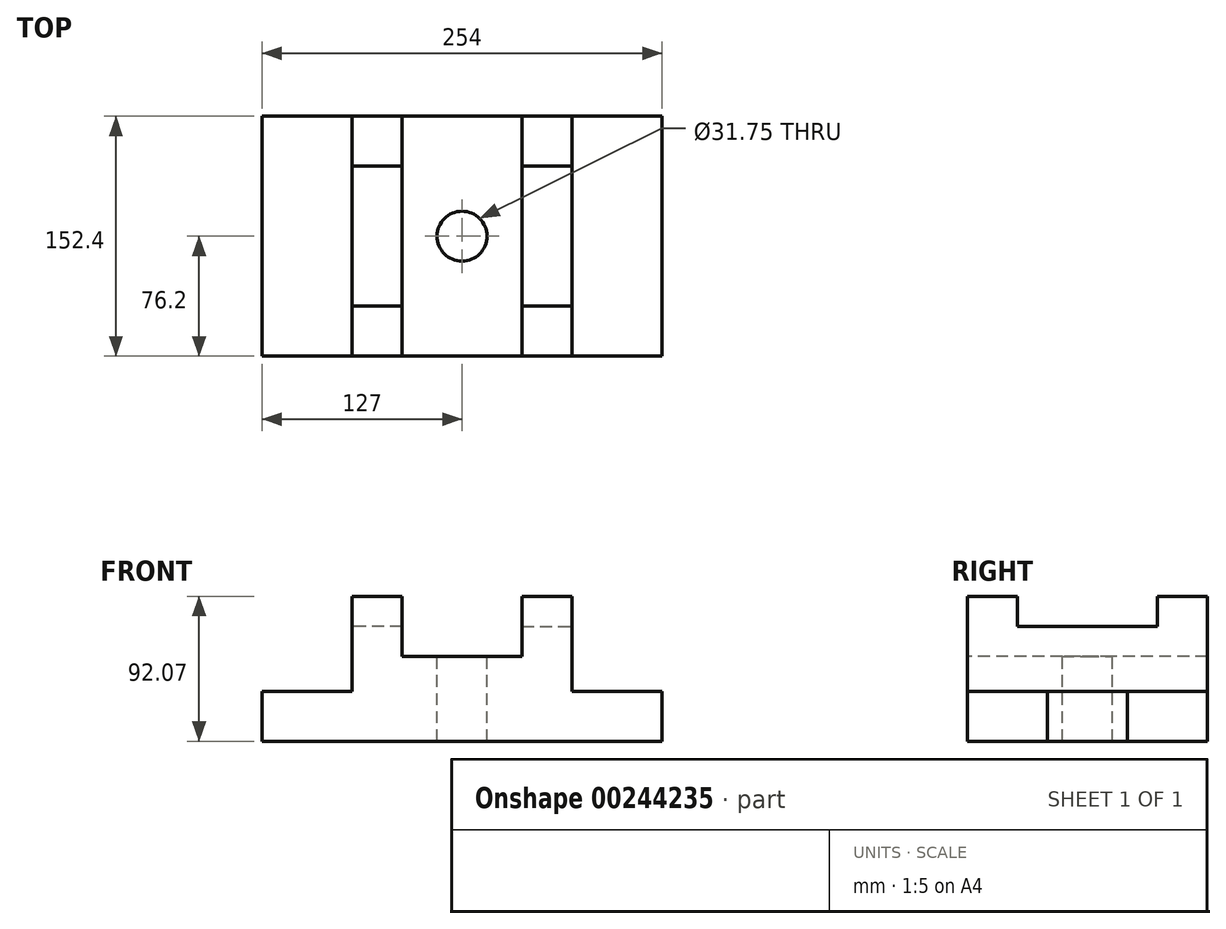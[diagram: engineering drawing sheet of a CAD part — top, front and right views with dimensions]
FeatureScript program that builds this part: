
annotation { "Feature Type Name" : "Feature", "Feature Type Description" : "" }
export const myFeature = defineFeature(function(context is Context, id is Id, definition is map)
    precondition{}
    {
        {
            var Q0;
            Q0=qCreatedBy(makeId("Front.planeOp"),FACE);
            var sketch = newSketch(context, id + "F0", { "sketchPlane" : qUnion([Q0])});
            skLineSegment(sketch, "E0.bottom", {"start": v(127, 15.88) * mm, "end": v(-127, 15.88) * mm});
            skLineSegment(sketch, "E0.top", {"start": v(127, -15.88) * mm, "end": v(-127, -15.88) * mm});
            skLineSegment(sketch, "E0.left", {"start": v(127, 15.88) * mm, "end": v(127, -15.88) * mm});
            skLineSegment(sketch, "E0.right", {"start": v(-127, 15.88) * mm, "end": v(-127, -15.88) * mm});
            skPoint(sketch, "E0.middle", {"position": v(0, 0) * mm});
            skSolve(sketch);
        }
        {
            var Q0;
            Q0=makeQuery(id+"F0.imprint","IMPRINT",FACE,{"disambiguationData":[TD([[makeQuery(id+"F0.imprint","IMPRINT",EDGE,{"derivedFrom":sQuery(id+"F0.wireOp",EDGE,"E0.bottom")}),1.0]])]});
            extrude(context, id + "F1", {"entities" : qUnion([Q0]), "depth" : 152.4 * mm});
        }
        {
            var Q0;
            Q0=makeQuery(id+"F1.opExtrude","SWEPT_FACE",FACE,{"disambiguationData":[OSD([sQuery(id+"F0.wireOp",EDGE,"E0.top")])]});
            extrude(context, id + "F2", {"entities" : qUnion([Q0]), "operationType" : NewBodyOperationType.ADD, "depth" : 92.07 * mm});
        }
        {
            var Q0;
            Q0=makeQuery(id+"F1.opExtrude","SWEPT_FACE",FACE,{"disambiguationData":[OSD([sQuery(id+"F0.wireOp",EDGE,"E0.bottom")])]});
            extrude(context, id + "F3", {"entities" : qUnion([Q0]), "operationType" : NewBodyOperationType.REMOVE, "oppositeDirection" : true, "depth" : 31.75 * mm});
        }
        {
            var Q0;
            Q0=makeQuery(id+"F3.boolean.opBoolean","COPY",FACE,{"derivedFrom":makeQuery(id+"F3.opExtrude","CAP_FACE",FACE,{"disambiguationData":[OSD([sQuery(id+"F0.wireOp",EDGE,"E0.bottom")])],"isStart":false})});
            var sketch = newSketch(context, id + "F4", { "sketchPlane" : qUnion([Q0])});
            skLineSegment(sketch, "E1", {"start": v(-127, 0) * mm, "end": v(-69.85, 0) * mm});
            skLineSegment(sketch, "E2", {"start": v(-69.85, -152.4) * mm, "end": v(-69.85, 0) * mm});
            skSolve(sketch);
        }
        {
            var Q0;
            Q0=makeQuery(id+"F4.imprint","IMPRINT",FACE,{"disambiguationData":[TD([[makeQuery(id+"F4.imprint","IMPRINT",EDGE,{"derivedFrom":sQuery(id+"F4.wireOp",EDGE,"E1")}),1.0]])]});
            extrude(context, id + "F5", {"entities" : qUnion([Q0]), "operationType" : NewBodyOperationType.REMOVE, "oppositeDirection" : true, "depth" : 59.05 * mm});
        }
        {
            var Q0;
            Q0=makeQuery(id+"F3.boolean.opBoolean","COPY",FACE,{"derivedFrom":makeQuery(id+"F3.opExtrude","CAP_FACE",FACE,{"disambiguationData":[OSD([sQuery(id+"F0.wireOp",EDGE,"E0.bottom")])],"isStart":false})});
            var sketch = newSketch(context, id + "F6", { "sketchPlane" : qUnion([Q0])});
            skLineSegment(sketch, "E3", {"start": v(-69.85, 0) * mm, "end": v(-38.1, 0) * mm});
            skLineSegment(sketch, "E4.bottom", {"start": v(-38.1, 0) * mm, "end": v(38.1, 0) * mm});
            skLineSegment(sketch, "E4.top", {"start": v(-38.1, -152.4) * mm, "end": v(38.1, -152.4) * mm});
            skLineSegment(sketch, "E4.left", {"start": v(-38.1, 0) * mm, "end": v(-38.1, -152.4) * mm});
            skLineSegment(sketch, "E4.right", {"start": v(38.1, 0) * mm, "end": v(38.1, -152.4) * mm});
            skSolve(sketch);
        }
        {
            var Q0;
            Q0=makeQuery(id+"F6.imprint","IMPRINT",FACE,{"disambiguationData":[TD([[makeQuery(id+"F6.imprint","IMPRINT",EDGE,{"derivedFrom":sQuery(id+"F6.wireOp",EDGE,"E4.bottom")}),1.0]])]});
            extrude(context, id + "F7", {"entities" : qUnion([Q0]), "operationType" : NewBodyOperationType.REMOVE, "oppositeDirection" : true, "depth" : 38.1 * mm});
        }
        {
            var Q0;
            {var subQ0=sQuery(id+"F0.wireOp",EDGE,"E0.left");var subQ3=sQuery(id+"F0.wireOp",EDGE,"E0.bottom");Q0=makeQuery(id+"F7.boolean.opBoolean","SPLIT",FACE,{"disambiguationData":[TD([makeQuery(id+"F1.opExtrude","SWEPT_FACE",FACE,{"disambiguationData":[OSD([subQ0])]})])],"derivedFrom":makeQuery(id+"F3.boolean.opBoolean","COPY",FACE,{"derivedFrom":makeQuery(id+"F3.opExtrude","CAP_FACE",FACE,{"disambiguationData":[OSD([subQ3])],"isStart":false})})});}
            var sketch = newSketch(context, id + "F8", { "sketchPlane" : qUnion([Q0])});
            skLineSegment(sketch, "E5", {"start": v(38.1, 0) * mm, "end": v(69.85, 0) * mm});
            skLineSegment(sketch, "E6.bottom", {"start": v(69.85, 0) * mm, "end": v(127, 0) * mm});
            skLineSegment(sketch, "E6.top", {"start": v(69.85, -152.4) * mm, "end": v(127, -152.4) * mm});
            skLineSegment(sketch, "E6.left", {"start": v(69.85, 0) * mm, "end": v(69.85, -152.4) * mm});
            skLineSegment(sketch, "E6.right", {"start": v(127, 0) * mm, "end": v(127, -152.4) * mm});
            skSolve(sketch);
        }
        {
            var Q0;
            Q0=makeQuery(id+"F8.imprint","IMPRINT",FACE,{"disambiguationData":[TD([[makeQuery(id+"F8.imprint","IMPRINT",EDGE,{"derivedFrom":sQuery(id+"F8.wireOp",EDGE,"E6.bottom")}),1.0]])]});
            extrude(context, id + "F9", {"entities" : qUnion([Q0]), "operationType" : NewBodyOperationType.REMOVE, "oppositeDirection" : true, "depth" : 60.32 * mm});
        }
        {
            var Q0;
            {var subQ0=sQuery(id+"F0.wireOp",EDGE,"E0.left");var subQ3=sQuery(id+"F0.wireOp",EDGE,"E0.bottom");Q0=makeQuery(id+"F7.boolean.opBoolean","SPLIT",FACE,{"disambiguationData":[TD([makeQuery(id+"F1.opExtrude","SWEPT_FACE",FACE,{"disambiguationData":[OSD([subQ0])]})])],"derivedFrom":makeQuery(id+"F3.boolean.opBoolean","COPY",FACE,{"derivedFrom":makeQuery(id+"F3.opExtrude","CAP_FACE",FACE,{"disambiguationData":[OSD([subQ3])],"isStart":false})})});}
            var sketch = newSketch(context, id + "F10", { "sketchPlane" : qUnion([Q0])});
            skLineSegment(sketch, "E7", {"start": v(38.1, -152.4) * mm, "end": v(38.1, -120.65) * mm});
            skLineSegment(sketch, "E8.bottom", {"start": v(38.1, -120.65) * mm, "end": v(69.85, -120.65) * mm});
            skLineSegment(sketch, "E8.top", {"start": v(38.1, -31.75) * mm, "end": v(69.85, -31.75) * mm});
            skLineSegment(sketch, "E8.left", {"start": v(38.1, -120.65) * mm, "end": v(38.1, -31.75) * mm});
            skLineSegment(sketch, "E8.right", {"start": v(69.85, -120.65) * mm, "end": v(69.85, -31.75) * mm});
            skSolve(sketch);
        }
        {
            var Q0;
            Q0=makeQuery(id+"F10.imprint","IMPRINT",FACE,{"disambiguationData":[TD([[makeQuery(id+"F10.imprint","IMPRINT",EDGE,{"derivedFrom":sQuery(id+"F10.wireOp",EDGE,"E8.bottom")}),1.0]])]});
            extrude(context, id + "F11", {"entities" : qUnion([Q0]), "operationType" : NewBodyOperationType.REMOVE, "oppositeDirection" : true, "depth" : 19.05 * mm});
        }
        {
            var Q0;
            {var subQ3=sQuery(id+"F0.wireOp",EDGE,"E0.bottom");Q0=makeQuery(id+"F7.boolean.opBoolean","SPLIT",FACE,{"disambiguationData":[TD([makeQuery(id+"F5.boolean.opBoolean","COPY",FACE,{"derivedFrom":makeQuery(id+"F5.opExtrude","SWEPT_FACE",FACE,{"disambiguationData":[OSD([sQuery(id+"F4.wireOp",EDGE,"E2")])]})})])],"derivedFrom":makeQuery(id+"F3.boolean.opBoolean","COPY",FACE,{"derivedFrom":makeQuery(id+"F3.opExtrude","CAP_FACE",FACE,{"disambiguationData":[OSD([subQ3])],"isStart":false})})});}
            var sketch = newSketch(context, id + "F12", { "sketchPlane" : qUnion([Q0])});
            skLineSegment(sketch, "E9", {"start": v(-38.1, 0) * mm, "end": v(-38.1, -31.75) * mm});
            skLineSegment(sketch, "E10.bottom", {"start": v(-38.1, -31.75) * mm, "end": v(-69.85, -31.75) * mm});
            skLineSegment(sketch, "E10.top", {"start": v(-38.1, -120.65) * mm, "end": v(-69.85, -120.65) * mm});
            skLineSegment(sketch, "E10.left", {"start": v(-38.1, -31.75) * mm, "end": v(-38.1, -120.65) * mm});
            skLineSegment(sketch, "E10.right", {"start": v(-69.85, -31.75) * mm, "end": v(-69.85, -120.65) * mm});
            skSolve(sketch);
        }
        {
            var Q0;
            Q0=makeQuery(id+"F12.imprint","IMPRINT",FACE,{"disambiguationData":[TD([[makeQuery(id+"F12.imprint","IMPRINT",EDGE,{"derivedFrom":sQuery(id+"F12.wireOp",EDGE,"E10.bottom")}),1.0]])]});
            extrude(context, id + "F13", {"entities" : qUnion([Q0]), "operationType" : NewBodyOperationType.REMOVE, "oppositeDirection" : true, "depth" : 19.05 * mm});
        }
        {
            var Q0;
            {var subQ0=sQuery(id+"F0.wireOp",EDGE,"E0.right");Q0=makeQuery(id+"F2.boolean.opBoolean","MERGE",FACE,{"derivedFrom":[makeQuery(id+"F1.opExtrude","SWEPT_FACE",FACE,{"disambiguationData":[OSD([subQ0])]}),makeQuery(id+"F2.opExtrude","SWEPT_FACE",FACE,{"disambiguationData":[OSD([sQuery(id+"F0.wireOp",EDGE,"E0.top"),subQ0])]})]});}
            var sketch = newSketch(context, id + "F14", { "sketchPlane" : qUnion([Q0])});
            skLineSegment(sketch, "E11", {"start": v(0, -74.93) * mm, "end": v(50.8, -74.93) * mm});
            skLineSegment(sketch, "E12.bottom", {"start": v(50.8, -74.93) * mm, "end": v(101.6, -74.93) * mm});
            skLineSegment(sketch, "E12.top", {"start": v(50.8, -107.95) * mm, "end": v(101.6, -107.95) * mm});
            skLineSegment(sketch, "E12.left", {"start": v(50.8, -74.93) * mm, "end": v(50.8, -107.95) * mm});
            skLineSegment(sketch, "E12.right", {"start": v(101.6, -74.93) * mm, "end": v(101.6, -107.95) * mm});
            skSolve(sketch);
        }
        {
            var Q0;
            Q0=makeQuery(id+"F14.imprint","IMPRINT",FACE,{"disambiguationData":[TD([[makeQuery(id+"F14.imprint","IMPRINT",EDGE,{"derivedFrom":sQuery(id+"F14.wireOp",EDGE,"E12.bottom")}),1.0]])]});
            extrude(context, id + "F15", {"entities" : qUnion([Q0]), "operationType" : NewBodyOperationType.REMOVE, "oppositeDirection" : true, "depth" : 13 / 203.2 * mm});
        }
        {
            var Q0;
            {var subQ0=sQuery(id+"F0.wireOp",EDGE,"E0.left");Q0=makeQuery(id+"F2.boolean.opBoolean","MERGE",FACE,{"derivedFrom":[makeQuery(id+"F1.opExtrude","SWEPT_FACE",FACE,{"disambiguationData":[OSD([subQ0])]}),makeQuery(id+"F2.opExtrude","SWEPT_FACE",FACE,{"disambiguationData":[OSD([sQuery(id+"F0.wireOp",EDGE,"E0.top"),subQ0])]})]});}
            var sketch = newSketch(context, id + "F16", { "sketchPlane" : qUnion([Q0])});
            skLineSegment(sketch, "E13", {"start": v(-152.4, -76.2) * mm, "end": v(-101.6, -76.2) * mm});
            skLineSegment(sketch, "E14.bottom", {"start": v(-101.6, -76.2) * mm, "end": v(-50.8, -76.2) * mm});
            skLineSegment(sketch, "E14.top", {"start": v(-101.6, -107.95) * mm, "end": v(-50.8, -107.95) * mm});
            skLineSegment(sketch, "E14.left", {"start": v(-101.6, -76.2) * mm, "end": v(-101.6, -107.95) * mm});
            skLineSegment(sketch, "E14.right", {"start": v(-50.8, -76.2) * mm, "end": v(-50.8, -107.95) * mm});
            skSolve(sketch);
        }
        {
            var Q0;
            Q0=makeQuery(id+"F16.imprint","IMPRINT",FACE,{"disambiguationData":[TD([[makeQuery(id+"F16.imprint","IMPRINT",EDGE,{"derivedFrom":sQuery(id+"F16.wireOp",EDGE,"E14.bottom")}),-1.0]])]});
            extrude(context, id + "F17", {"entities" : qUnion([Q0]), "operationType" : NewBodyOperationType.REMOVE, "oppositeDirection" : true, "depth" : 13 / 203.2 * mm});
        }
        {
            var Q0;
            Q0=makeQuery(id+"F7.boolean.opBoolean","COPY",FACE,{"derivedFrom":makeQuery(id+"F7.opExtrude","CAP_FACE",FACE,{"disambiguationData":[OSD([sQuery(id+"F6.wireOp",EDGE,"E4.bottom"),sQuery(id+"F6.wireOp",EDGE,"E4.top"),sQuery(id+"F6.wireOp",EDGE,"E4.left"),sQuery(id+"F6.wireOp",EDGE,"E4.right")])],"isStart":false})});
            var sketch = newSketch(context, id + "F18", { "sketchPlane" : qUnion([Q0])});
            skLineSegment(sketch, "E15", {"start": v(0, -152.4) * mm, "end": v(0, -76.2) * mm, "construction": true});
            skCircle(sketch, "E16", {"center": v(0, -76.2) * mm, "radius": 15.88 * mm});
            skSolve(sketch);
        }
        {
            var Q0;
            Q0=makeQuery(id+"F18.imprint","IMPRINT",FACE,{"disambiguationData":[TD([[makeQuery(id+"F18.imprint","IMPRINT",EDGE,{"derivedFrom":sQuery(id+"F18.wireOp",EDGE,"E16")}),1.0]])]});
            extrude(context, id + "F19", {"entities" : qUnion([Q0]), "operationType" : NewBodyOperationType.REMOVE, "endBound" : BoundingType.THROUGH_ALL, "oppositeDirection" : true, "depth" : 25.4 * mm});
        }
        {
            var Q0;
            Q0=makeQuery(id+"F5.boolean.opBoolean","COPY",FACE,{"derivedFrom":makeQuery(id+"F5.opExtrude","CAP_FACE",FACE,{"disambiguationData":[OSD([sQuery(id+"F0.wireOp",EDGE,"E0.bottom"),sQuery(id+"F0.wireOp",EDGE,"E0.right"),sQuery(id+"F4.wireOp",EDGE,"E1"),sQuery(id+"F4.wireOp",EDGE,"E2")])],"isStart":false})});
            extrude(context, id + "F20", {"entities" : qUnion([Q0]), "operationType" : NewBodyOperationType.REMOVE, "oppositeDirection" : true, "depth" : 1.27 * mm});
        }
    });
